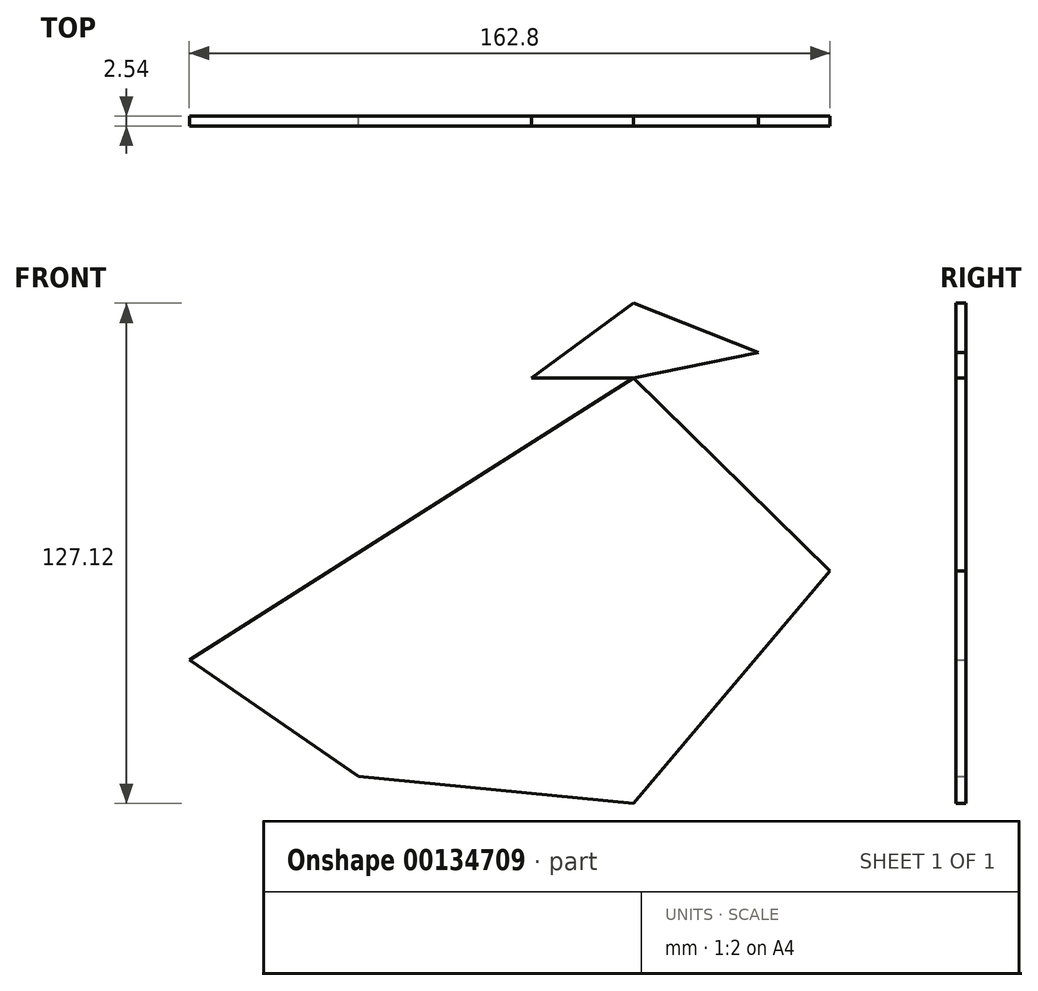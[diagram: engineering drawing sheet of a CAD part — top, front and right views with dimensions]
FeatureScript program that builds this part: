
annotation { "Feature Type Name" : "Feature", "Feature Type Description" : "" }
export const myFeature = defineFeature(function(context is Context, id is Id, definition is map)
    precondition{}
    {
        {
            var Q0;
            Q0=qCreatedBy(makeId("Front.planeOp"),FACE);
            var sketch = newSketch(context, id + "F0", { "sketchPlane" : qUnion([Q0])});
            skLineSegment(sketch, "E0", {"start": v(20.25, 62.61) * mm, "end": v(20.25, -45.5) * mm});
            skLineSegment(sketch, "E1", {"start": v(20.25, -45.5) * mm, "end": v(70.17, 13.55) * mm});
            skLineSegment(sketch, "E2", {"start": v(70.17, 13.55) * mm, "end": v(20.25, 62.61) * mm});
            skLineSegment(sketch, "E3", {"start": v(20.25, 62.61) * mm, "end": v(-49.63, -38.65) * mm});
            skLineSegment(sketch, "E4", {"start": v(-49.63, -38.65) * mm, "end": v(20.25, -45.5) * mm});
            skLineSegment(sketch, "E5", {"start": v(20.25, 81.62) * mm, "end": v(20.25, 62.61) * mm});
            skLineSegment(sketch, "E6", {"start": v(20.25, 81.62) * mm, "end": v(51.93, 69.07) * mm});
            skLineSegment(sketch, "E7", {"start": v(51.93, 69.07) * mm, "end": v(20.25, 62.61) * mm});
            skLineSegment(sketch, "E8", {"start": v(20.25, 62.61) * mm, "end": v(-5.73, 62.61) * mm});
            skLineSegment(sketch, "E9", {"start": v(-5.73, 62.61) * mm, "end": v(20.25, 81.62) * mm});
            skLineSegment(sketch, "E10", {"start": v(-49.63, -38.65) * mm, "end": v(-92.63, -8.98) * mm});
            skLineSegment(sketch, "E11", {"start": v(-92.63, -8.98) * mm, "end": v(20.25, 62.61) * mm});
            skSolve(sketch);
        }
        {
            var Q0;
            Q0 = qSketchRegion(id + "F0", true);
            extrude(context, id + "F1", {"entities" : qUnion([Q0]), "depth" : 2.54 * mm});
        }
    });
